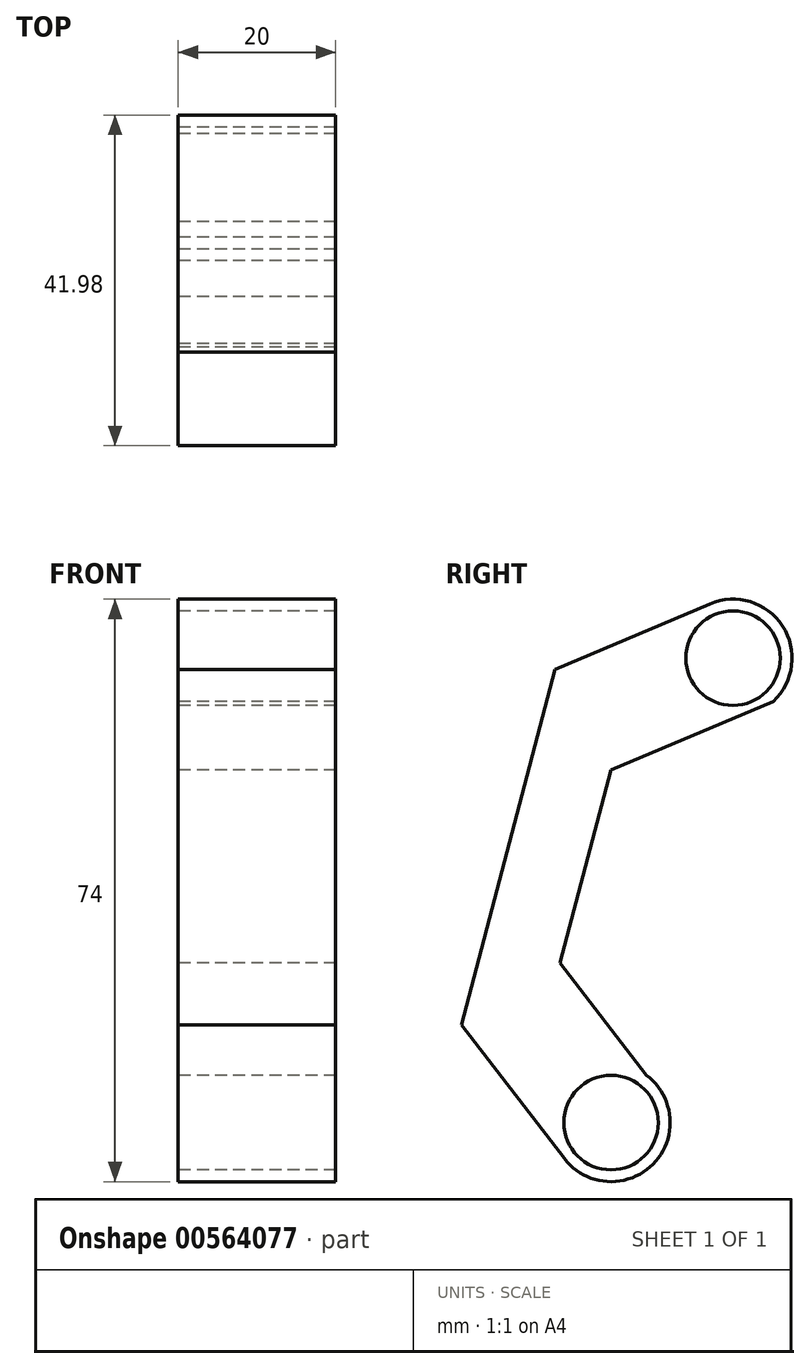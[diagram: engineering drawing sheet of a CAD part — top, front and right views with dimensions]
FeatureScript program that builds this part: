
annotation { "Feature Type Name" : "Feature", "Feature Type Description" : "" }
export const myFeature = defineFeature(function(context is Context, id is Id, definition is map)
    precondition{}
    {
        {
            var Q0;
            Q0=qCreatedBy(makeId("Right.planeOp"),FACE);
            var sketch = newSketch(context, id + "F0", { "sketchPlane" : qUnion([Q0])});
            skLineSegment(sketch, "E0", {"start": v(0, 0) * mm, "end": v(15.5, 59) * mm, "construction": true});
            skLineSegment(sketch, "E1", {"start": v(0, 0) * mm, "end": v(0, 59) * mm, "construction": true});
            skLineSegment(sketch, "E2", {"start": v(0, 59) * mm, "end": v(15.5, 59) * mm, "construction": true});
            skLineSegment(sketch, "E3", {"start": v(0, 0) * mm, "end": v(-13.3, 17.32) * mm, "construction": true});
            skLineSegment(sketch, "E4", {"start": v(-13.3, 17.32) * mm, "end": v(-4.59, 50.5) * mm, "construction": true});
            skLineSegment(sketch, "E5", {"start": v(-4.59, 50.5) * mm, "end": v(15.5, 59) * mm, "construction": true});
            skCircle(sketch, "E6", {"center": v(0, 0) * mm, "radius": 6 * mm});
            skCircle(sketch, "E7", {"center": v(15.5, 59) * mm, "radius": 6 * mm});
            skLineSegment(sketch, "E8", {"start": v(12.57, 65.9) * mm, "end": v(-7.13, 57.58) * mm});
            skLineSegment(sketch, "E9", {"start": v(-7.13, 57.58) * mm, "end": v(-18.99, 12.42) * mm});
            skLineSegment(sketch, "E10", {"start": v(-18.99, 12.42) * mm, "end": v(-5.95, -4.57) * mm});
            skLineSegment(sketch, "E11", {"start": v(20.62, 53.53) * mm, "end": v(-0.03, 44.8) * mm});
            skLineSegment(sketch, "E12", {"start": v(-0.03, 44.8) * mm, "end": v(-6.47, 20.3) * mm});
            skLineSegment(sketch, "E13", {"start": v(-6.47, 20.3) * mm, "end": v(4.5, 6) * mm});
            skArc(sketch, "E14", {"start": v(12.57, 65.9) * mm, "mid": v(21.78, 63.09) * mm, "end": v(20.62, 53.53) * mm});
            skArc(sketch, "E15", {"start": v(-5.95, -4.57) * mm, "mid": v(5.33, -5.28) * mm, "end": v(4.5, 6) * mm});
            skSolve(sketch);
        }
        {
            var Q0;
            Q0 = qSketchRegion(id + "F0", true);
            extrude(context, id + "F1", {"entities" : qUnion([Q0]), "depth" : 20 * mm, "offsetDistance" : 25 * mm});
        }
    });
